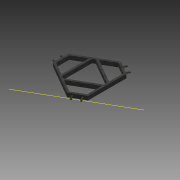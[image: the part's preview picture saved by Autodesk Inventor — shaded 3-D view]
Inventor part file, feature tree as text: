
AUTODESK INVENTOR PART (.ipt)
format: ipt  version: 2015 SP1 (Build 190203100, 203)  size: 179,712 bytes
history: native  units: in
note: dims shown in document units (in); Inventor stores cm internally (conversion verified against a paired STEP export)
features: projected_geometry x8, sketch x7, extrude x4, other x3, revolve x3
ambient origin geometry x8: Origin, YZ Plane, XZ Plane, XY Plane, X Axis, Y Axis, Z Axis, Center Point
bodies: Solid1 (feature_tree)
feature tree (25):
  extrude  "Extrusion1"  Depth=20.0in
  extrude  "Extrusion2"  Depth=15.5in
  extrude  "Extrusion3"  Depth=2.0in TaperAngle=0.0deg
  extrude  "Extrusion4"  Depth=2.0in
  sketch  "Sketch5"  dims[d25=0.75in d26=0.75in]
  other  "Work Axis2"
  revolve  "Revolution1"  [1 undecoded]
  sketch  "Sketch6"  dims[d27=2.0in d28=0.0in d29=2.0in]
  other  "Work Axis3"
  revolve  "Revolution2"  [1 undecoded]
  sketch  "Sketch7"  dims[d30=2.0in d31=0.75in d32=0.75in d33=2.0in d34=0.0in d35=2.0in d36=2.0in d37=0.75in d38=0.75in d39=2.0in d40=0.0in d47=90.0deg d50=90.0deg d53=90.0deg]
  other  "Work Axis4"
  revolve  "Revolution3"  [1 undecoded]
  sketch  "Sketch1"  dims[d0=8.0in d6=20.0in]
  sketch  "Sketch2"  dims[d14=15.5in d16=15.5in]
  projected_geometry  "Projected Loop1"
  sketch  "Sketch3"  dims[d17=15.5in d21=2.0in d22=0.0in]
  projected_geometry  "Projected Loop2"
  sketch  "Sketch4"  dims[d23=2.0in d24=2.0in]
  projected_geometry  "Projected Loop3"
  projected_geometry  "Projected Loop4"
  projected_geometry  "Projected Loop5"
  projected_geometry  "Projected Loop6"
  projected_geometry  "Projected Loop7"
  projected_geometry  "Projected Loop8"
note: 3 required parameter values undecoded (feature->parameter linkage not recoverable at this tier; creation-order binding heuristic only, values carry confidence <= 0.55)
